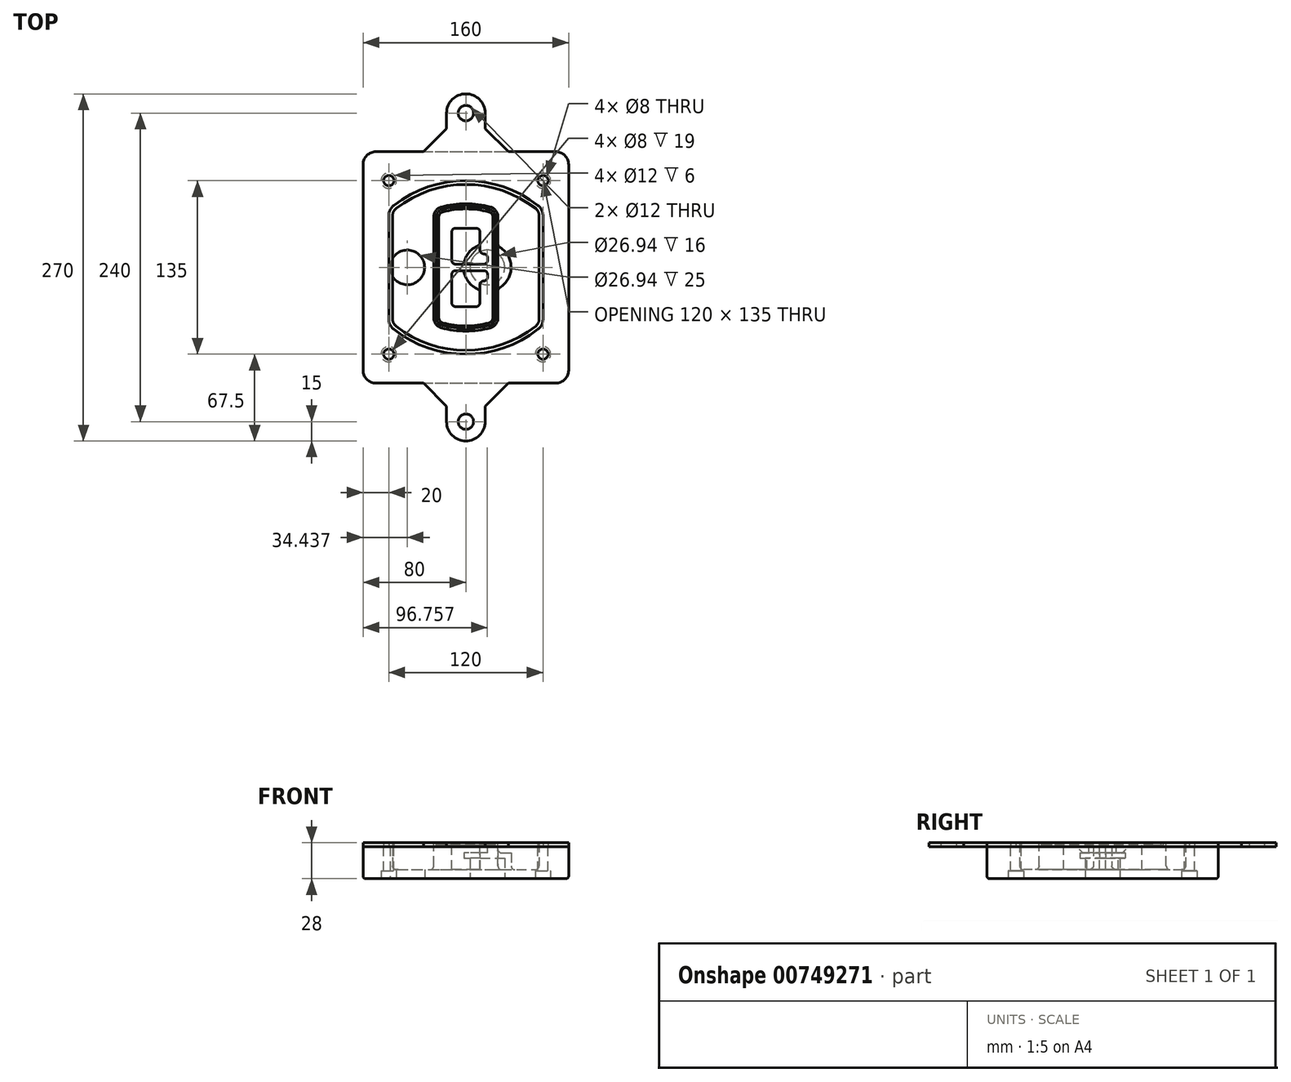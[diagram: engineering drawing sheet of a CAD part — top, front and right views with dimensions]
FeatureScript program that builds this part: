
annotation { "Feature Type Name" : "Feature", "Feature Type Description" : "" }
export const myFeature = defineFeature(function(context is Context, id is Id, definition is map)
    precondition{}
    {
        {
            var Q0;
            Q0=qCreatedBy(makeId("Top.planeOp"),FACE);
            var sketch = newSketch(context, id + "F0", { "sketchPlane" : qUnion([Q0])});
            skPoint(sketch, "E0.rect.middle", {"position": v(0, 0) * mm});
            skLineSegment(sketch, "E1.bottom", {"start": v(-70, -90) * mm, "end": v(70, -90) * mm});
            skLineSegment(sketch, "E1.top", {"start": v(-70, 90) * mm, "end": v(70, 90) * mm});
            skLineSegment(sketch, "E1.left", {"start": v(-80, -80) * mm, "end": v(-80, 80) * mm});
            skLineSegment(sketch, "E1.right", {"start": v(80, -80) * mm, "end": v(80, 80) * mm});
            skLineSegment(sketch, "E2", {"start": v(-80, 90) * mm, "end": v(80, -90) * mm, "construction": true});
            skLineSegment(sketch, "E3", {"start": v(80, 90) * mm, "end": v(-80, -90) * mm, "construction": true});
            skCircle(sketch, "E4", {"center": v(-60, 67.5) * mm, "radius": 4 * mm});
            skCircle(sketch, "E5", {"center": v(60, 67.5) * mm, "radius": 4 * mm});
            skCircle(sketch, "E6", {"center": v(60, -67.5) * mm, "radius": 4 * mm});
            skCircle(sketch, "E7", {"center": v(-60, -67.5) * mm, "radius": 4 * mm});
            skLineSegment(sketch, "E8", {"start": v(-60, 67.5) * mm, "end": v(60, 67.5) * mm, "construction": true});
            skLineSegment(sketch, "E9", {"start": v(60, 67.5) * mm, "end": v(60, -67.5) * mm, "construction": true});
            skLineSegment(sketch, "E10", {"start": v(60, -67.5) * mm, "end": v(-60, -67.5) * mm, "construction": true});
            skLineSegment(sketch, "E11", {"start": v(-60, -67.5) * mm, "end": v(-60, 67.5) * mm, "construction": true});
            skLineSegment(sketch, "E12", {"start": v(-60, 40.3) * mm, "end": v(-60, -40.3) * mm});
            skLineSegment(sketch, "E13", {"start": v(60, 40.3) * mm, "end": v(60, -40.3) * mm});
            skArc(sketch, "E14", {"start": v(56.15, 48.18) * mm, "mid": v(0, 67.5) * mm, "end": v(-56.15, 48.18) * mm});
            skArc(sketch, "E15", {"start": v(-56.15, -48.18) * mm, "mid": v(0, -67.5) * mm, "end": v(56.15, -48.18) * mm});
            skLineSegment(sketch, "E16", {"start": v(-60, 0) * mm, "end": v(60, 0) * mm, "construction": true});
            skPoint(sketch, "E17.visualSharp", {"position": v(-60, -45) * mm});
            skArc(sketch, "E17.filletArc", {"start": v(-60, -40.3) * mm, "mid": v(-58.99, -44.68) * mm, "end": v(-56.15, -48.18) * mm});
            skPoint(sketch, "E18.visualSharp", {"position": v(-60, 45) * mm});
            skArc(sketch, "E18.filletArc", {"start": v(-56.15, 48.18) * mm, "mid": v(-58.99, 44.68) * mm, "end": v(-60, 40.3) * mm});
            skPoint(sketch, "E19.visualSharp", {"position": v(60, 45) * mm});
            skArc(sketch, "E19.filletArc", {"start": v(60, 40.3) * mm, "mid": v(58.99, 44.68) * mm, "end": v(56.15, 48.18) * mm});
            skPoint(sketch, "E20.visualSharp", {"position": v(60, -45) * mm});
            skArc(sketch, "E20.filletArc", {"start": v(56.15, -48.18) * mm, "mid": v(58.99, -44.68) * mm, "end": v(60, -40.3) * mm});
            skPoint(sketch, "E21.visualSharp", {"position": v(-80, 90) * mm});
            skArc(sketch, "E21.filletArc", {"start": v(-70, 90) * mm, "mid": v(-77.07, 87.07) * mm, "end": v(-80, 80) * mm});
            skPoint(sketch, "E22.visualSharp", {"position": v(80, 90) * mm});
            skArc(sketch, "E22.filletArc", {"start": v(80, 80) * mm, "mid": v(77.07, 87.07) * mm, "end": v(70, 90) * mm});
            skPoint(sketch, "E23.visualSharp", {"position": v(80, -90) * mm});
            skArc(sketch, "E23.filletArc", {"start": v(70, -90) * mm, "mid": v(77.07, -87.07) * mm, "end": v(80, -80) * mm});
            skPoint(sketch, "E24.visualSharp", {"position": v(-80, -90) * mm});
            skArc(sketch, "E24.filletArc", {"start": v(-80, -80) * mm, "mid": v(-77.07, -87.07) * mm, "end": v(-70, -90) * mm});
            skArc(sketch, "E25.0", {"start": v(57, 40.3) * mm, "mid": v(56.3, 43.36) * mm, "end": v(54.3, 45.81) * mm});
            skLineSegment(sketch, "E25.1", {"start": v(57, 40.3) * mm, "end": v(57, -40.3) * mm});
            skArc(sketch, "E25.2", {"start": v(54.3, -45.81) * mm, "mid": v(56.3, -43.36) * mm, "end": v(57, -40.3) * mm});
            skArc(sketch, "E25.3", {"start": v(-54.3, -45.81) * mm, "mid": v(0, -64.5) * mm, "end": v(54.3, -45.81) * mm});
            skArc(sketch, "E25.4", {"start": v(-57, -40.3) * mm, "mid": v(-56.3, -43.36) * mm, "end": v(-54.3, -45.81) * mm});
            skArc(sketch, "E25.5", {"start": v(54.3, 45.81) * mm, "mid": v(0, 64.5) * mm, "end": v(-54.3, 45.81) * mm});
            skLineSegment(sketch, "E25.6", {"start": v(-57, 40.3) * mm, "end": v(-57, -40.3) * mm});
            skArc(sketch, "E25.7", {"start": v(-54.3, 45.81) * mm, "mid": v(-56.3, 43.36) * mm, "end": v(-57, 40.3) * mm});
            skArc(sketch, "E26.0", {"start": v(-58.62, 51.33) * mm, "mid": v(-62.58, 46.43) * mm, "end": v(-64, 40.3) * mm});
            skArc(sketch, "E26.1", {"start": v(58.62, 51.33) * mm, "mid": v(0, 71.5) * mm, "end": v(-58.62, 51.33) * mm});
            skArc(sketch, "E26.2", {"start": v(64, 40.3) * mm, "mid": v(62.58, 46.43) * mm, "end": v(58.62, 51.33) * mm});
            skLineSegment(sketch, "E26.3", {"start": v(64, 40.3) * mm, "end": v(64, -40.3) * mm});
            skArc(sketch, "E26.4", {"start": v(58.62, -51.33) * mm, "mid": v(62.58, -46.43) * mm, "end": v(64, -40.3) * mm});
            skLineSegment(sketch, "E26.5", {"start": v(-64, 40.3) * mm, "end": v(-64, -40.3) * mm});
            skArc(sketch, "E26.6", {"start": v(-58.62, -51.33) * mm, "mid": v(0, -71.5) * mm, "end": v(58.62, -51.33) * mm});
            skArc(sketch, "E26.7", {"start": v(-64, -40.3) * mm, "mid": v(-62.58, -46.43) * mm, "end": v(-58.62, -51.33) * mm});
            skSolve(sketch);
        }
        {
            var Q0;
            Q0=makeQuery(id+"F0.imprint","IMPRINT",FACE,{"disambiguationData":[TD([[makeQuery(id+"F0.imprint","IMPRINT",EDGE,{"derivedFrom":sQuery(id+"F0.wireOp",EDGE,"E1.bottom")}),1.0]])]});
            var Q1;
            Q1=makeQuery(id+"F0.imprint","IMPRINT",FACE,{"disambiguationData":[TD([[makeQuery(id+"F0.imprint","IMPRINT",EDGE,{"derivedFrom":sQuery(id+"F0.wireOp",EDGE,"E12")}),1.0]])]});
            var Q2;
            Q2=makeQuery(id+"F0.imprint","IMPRINT",FACE,{"disambiguationData":[TD([[makeQuery(id+"F0.imprint","IMPRINT",EDGE,{"derivedFrom":sQuery(id+"F0.wireOp",EDGE,"E25.0")}),1.0]])]});
            var Q3;
            Q3=makeQuery(id+"F0.imprint","IMPRINT",FACE,{"disambiguationData":[TD([[makeQuery(id+"F0.imprint","IMPRINT",EDGE,{"derivedFrom":sQuery(id+"F0.wireOp",EDGE,"E12")}),-1.0]])]});
            extrude(context, id + "F1", {"entities" : qUnion([Q0, Q1, Q2, Q3]), "oppositeDirection" : true, "depth" : 25 * mm});
        }
        {
            var Q0;
            Q0=makeQuery(id+"F0.imprint","IMPRINT",FACE,{"disambiguationData":[TD([[makeQuery(id+"F0.imprint","IMPRINT",EDGE,{"derivedFrom":sQuery(id+"F0.wireOp",EDGE,"E12")}),1.0]])]});
            extrude(context, id + "F2", {"entities" : qUnion([Q0]), "operationType" : NewBodyOperationType.ADD, "depth" : 3 * mm});
        }
        {
            var Q0;
            Q0=makeQuery(id+"F0.imprint","IMPRINT",FACE,{"disambiguationData":[TD([[makeQuery(id+"F0.imprint","IMPRINT",EDGE,{"derivedFrom":sQuery(id+"F0.wireOp",EDGE,"E25.0")}),1.0]])]});
            extrude(context, id + "F3", {"entities" : qUnion([Q0]), "operationType" : NewBodyOperationType.REMOVE, "oppositeDirection" : true, "depth" : 18 * mm});
        }
        {
            var Q0;
            Q0=makeQuery(id+"F2.opExtrude","CAP_FACE",FACE,{"disambiguationData":[OSD([sQuery(id+"F0.wireOp",EDGE,"E12"),sQuery(id+"F0.wireOp",EDGE,"E13"),sQuery(id+"F0.wireOp",EDGE,"E14"),sQuery(id+"F0.wireOp",EDGE,"E15"),sQuery(id+"F0.wireOp",EDGE,"E17.filletArc"),sQuery(id+"F0.wireOp",EDGE,"E18.filletArc"),sQuery(id+"F0.wireOp",EDGE,"E19.filletArc"),sQuery(id+"F0.wireOp",EDGE,"E20.filletArc"),sQuery(id+"F0.wireOp",EDGE,"E25.0"),sQuery(id+"F0.wireOp",EDGE,"E25.1"),sQuery(id+"F0.wireOp",EDGE,"E25.2"),sQuery(id+"F0.wireOp",EDGE,"E25.3"),sQuery(id+"F0.wireOp",EDGE,"E25.4"),sQuery(id+"F0.wireOp",EDGE,"E25.5"),sQuery(id+"F0.wireOp",EDGE,"E25.6"),sQuery(id+"F0.wireOp",EDGE,"E25.7")])],"isStart":false});
            var sketch = newSketch(context, id + "F4", { "sketchPlane" : qUnion([Q0])});
            skArc(sketch, "E27.0", {"start": v(-19.08, -46.97) * mm, "mid": v(0, -49.5) * mm, "end": v(19.08, -46.97) * mm});
            skArc(sketch, "E28.0", {"start": v(19.08, 46.97) * mm, "mid": v(0, 49.5) * mm, "end": v(-19.08, 46.97) * mm});
            skLineSegment(sketch, "E29", {"start": v(-25, 39.25) * mm, "end": v(-25, -39.25) * mm});
            skLineSegment(sketch, "E30", {"start": v(25, 39.25) * mm, "end": v(25, -39.25) * mm});
            skLineSegment(sketch, "E31", {"start": v(-25, 45.1) * mm, "end": v(25, 45.1) * mm, "construction": true});
            skLineSegment(sketch, "E32", {"start": v(-25, -45.1) * mm, "end": v(25, -45.1) * mm, "construction": true});
            skPoint(sketch, "E33.visualSharp", {"position": v(-25, 45.1) * mm});
            skArc(sketch, "E33.filletArc", {"start": v(-19.08, 46.97) * mm, "mid": v(-23.35, 44.11) * mm, "end": v(-25, 39.25) * mm});
            skPoint(sketch, "E34.visualSharp", {"position": v(25, 45.1) * mm});
            skArc(sketch, "E34.filletArc", {"start": v(25, 39.25) * mm, "mid": v(23.35, 44.11) * mm, "end": v(19.08, 46.97) * mm});
            skPoint(sketch, "E35.visualSharp", {"position": v(25, -45.1) * mm});
            skArc(sketch, "E35.filletArc", {"start": v(19.08, -46.97) * mm, "mid": v(23.35, -44.11) * mm, "end": v(25, -39.25) * mm});
            skPoint(sketch, "E36.visualSharp", {"position": v(-25, -45.1) * mm});
            skArc(sketch, "E36.filletArc", {"start": v(-25, -39.25) * mm, "mid": v(-23.35, -44.11) * mm, "end": v(-19.08, -46.97) * mm});
            skArc(sketch, "E37.0", {"start": v(54.3, 45.81) * mm, "mid": v(0, 64.5) * mm, "end": v(-54.3, 45.81) * mm});
            skArc(sketch, "E37.1", {"start": v(-54.3, 45.81) * mm, "mid": v(-56.3, 43.36) * mm, "end": v(-57, 40.3) * mm});
            skLineSegment(sketch, "E37.2", {"start": v(-57, 40.3) * mm, "end": v(-57, -40.3) * mm});
            skArc(sketch, "E37.3", {"start": v(-57, -40.3) * mm, "mid": v(-56.3, -43.36) * mm, "end": v(-54.3, -45.81) * mm});
            skArc(sketch, "E37.4", {"start": v(-54.3, -45.81) * mm, "mid": v(0, -64.5) * mm, "end": v(54.3, -45.81) * mm});
            skArc(sketch, "E37.5", {"start": v(54.3, -45.81) * mm, "mid": v(56.3, -43.36) * mm, "end": v(57, -40.3) * mm});
            skLineSegment(sketch, "E37.6", {"start": v(57, 40.3) * mm, "end": v(57, -40.3) * mm});
            skArc(sketch, "E37.7", {"start": v(57, 40.3) * mm, "mid": v(56.3, 43.36) * mm, "end": v(54.3, 45.81) * mm});
            skLineSegment(sketch, "E38.0", {"start": v(23, 39.25) * mm, "end": v(23, -39.25) * mm});
            skArc(sketch, "E38.1", {"start": v(18.56, -45.04) * mm, "mid": v(21.76, -42.9) * mm, "end": v(23, -39.25) * mm});
            skArc(sketch, "E38.2", {"start": v(-18.56, -45.04) * mm, "mid": v(0, -47.5) * mm, "end": v(18.56, -45.04) * mm});
            skArc(sketch, "E38.3", {"start": v(-23, -39.25) * mm, "mid": v(-21.76, -42.9) * mm, "end": v(-18.56, -45.04) * mm});
            skLineSegment(sketch, "E38.4", {"start": v(-23, 39.25) * mm, "end": v(-23, -39.25) * mm});
            skArc(sketch, "E38.5", {"start": v(23, 39.25) * mm, "mid": v(21.76, 42.9) * mm, "end": v(18.56, 45.04) * mm});
            skArc(sketch, "E38.6", {"start": v(-18.56, 45.04) * mm, "mid": v(-21.76, 42.9) * mm, "end": v(-23, 39.25) * mm});
            skArc(sketch, "E38.7", {"start": v(18.56, 45.04) * mm, "mid": v(0, 47.5) * mm, "end": v(-18.56, 45.04) * mm});
            skArc(sketch, "E39.0", {"start": v(21, 39.25) * mm, "mid": v(20.18, 41.68) * mm, "end": v(18.04, 43.1) * mm});
            skLineSegment(sketch, "E39.1", {"start": v(21, 39.25) * mm, "end": v(21, -39.25) * mm});
            skArc(sketch, "E39.2", {"start": v(18.04, -43.1) * mm, "mid": v(20.18, -41.68) * mm, "end": v(21, -39.25) * mm});
            skArc(sketch, "E39.3", {"start": v(-18.04, -43.1) * mm, "mid": v(0, -45.5) * mm, "end": v(18.04, -43.1) * mm});
            skArc(sketch, "E39.4", {"start": v(-21, -39.25) * mm, "mid": v(-20.18, -41.68) * mm, "end": v(-18.04, -43.1) * mm});
            skArc(sketch, "E39.5", {"start": v(18.04, 43.1) * mm, "mid": v(0, 45.5) * mm, "end": v(-18.04, 43.1) * mm});
            skLineSegment(sketch, "E39.6", {"start": v(-21, 39.25) * mm, "end": v(-21, -39.25) * mm});
            skArc(sketch, "E39.7", {"start": v(-18.04, 43.1) * mm, "mid": v(-20.18, 41.68) * mm, "end": v(-21, 39.25) * mm});
            skLineSegment(sketch, "E40", {"start": v(-25, 0) * mm, "end": v(25, 0) * mm, "construction": true});
            skLineSegment(sketch, "E41", {"start": v(-11, 5.5) * mm, "end": v(-11, 27.5) * mm});
            skLineSegment(sketch, "E42", {"start": v(-8, 30.5) * mm, "end": v(8, 30.5) * mm});
            skLineSegment(sketch, "E43", {"start": v(11, 27.5) * mm, "end": v(11, 13.5) * mm});
            skLineSegment(sketch, "E44", {"start": v(14, 10.5) * mm, "end": v(14, 10.5) * mm});
            skLineSegment(sketch, "E45", {"start": v(17, 7.5) * mm, "end": v(17, 5.5) * mm});
            skLineSegment(sketch, "E46", {"start": v(14, 2.5) * mm, "end": v(-8, 2.5) * mm});
            skPoint(sketch, "E47.visualSharp", {"position": v(-11, 30.5) * mm});
            skArc(sketch, "E47.filletArc", {"start": v(-8, 30.5) * mm, "mid": v(-10.12, 29.62) * mm, "end": v(-11, 27.5) * mm});
            skPoint(sketch, "E48.visualSharp", {"position": v(11, 30.5) * mm});
            skArc(sketch, "E48.filletArc", {"start": v(11, 27.5) * mm, "mid": v(10.12, 29.62) * mm, "end": v(8, 30.5) * mm});
            skPoint(sketch, "E49.visualSharp", {"position": v(11, 10.5) * mm});
            skArc(sketch, "E49.filletArc", {"start": v(11, 13.5) * mm, "mid": v(11.88, 11.38) * mm, "end": v(14, 10.5) * mm});
            skPoint(sketch, "E50.visualSharp", {"position": v(17, 10.5) * mm});
            skArc(sketch, "E50.filletArc", {"start": v(17, 7.5) * mm, "mid": v(16.12, 9.62) * mm, "end": v(14, 10.5) * mm});
            skPoint(sketch, "E51.visualSharp", {"position": v(17, 2.5) * mm});
            skArc(sketch, "E51.filletArc", {"start": v(14, 2.5) * mm, "mid": v(16.12, 3.38) * mm, "end": v(17, 5.5) * mm});
            skPoint(sketch, "E52.visualSharp", {"position": v(-11, 2.5) * mm});
            skArc(sketch, "E52.filletArc", {"start": v(-11, 5.5) * mm, "mid": v(-10.12, 3.38) * mm, "end": v(-8, 2.5) * mm});
            skLineSegment(sketch, "E53.0.MirrorCS", {"start": v(14, -2.5) * mm, "end": v(-8, -2.5) * mm});
            skArc(sketch, "E54.0.MirrorCS", {"start": v(-11, -5.5) * mm, "mid": v(-10.12, -3.38) * mm, "end": v(-8, -2.5) * mm});
            skLineSegment(sketch, "E55.0.MirrorCS", {"start": v(-11, -5.5) * mm, "end": v(-11, -27.5) * mm});
            skArc(sketch, "E56.0.MirrorCS", {"start": v(-8, -30.5) * mm, "mid": v(-10.12, -29.62) * mm, "end": v(-11, -27.5) * mm});
            skLineSegment(sketch, "E57.0.MirrorCS", {"start": v(-8, -30.5) * mm, "end": v(8, -30.5) * mm});
            skArc(sketch, "E58.0.MirrorCS", {"start": v(11, -27.5) * mm, "mid": v(10.12, -29.62) * mm, "end": v(8, -30.5) * mm});
            skLineSegment(sketch, "E59.0.MirrorCS", {"start": v(11, -27.5) * mm, "end": v(11, -13.5) * mm});
            skArc(sketch, "E60.0.MirrorCS", {"start": v(11, -13.5) * mm, "mid": v(11.88, -11.38) * mm, "end": v(14, -10.5) * mm});
            skArc(sketch, "E61.0.MirrorCS", {"start": v(17, -7.5) * mm, "mid": v(16.12, -9.62) * mm, "end": v(14, -10.5) * mm});
            skLineSegment(sketch, "E62.0.MirrorCS", {"start": v(17, -7.5) * mm, "end": v(17, -5.5) * mm});
            skArc(sketch, "E63.0.MirrorCS", {"start": v(14, -2.5) * mm, "mid": v(16.12, -3.38) * mm, "end": v(17, -5.5) * mm});
            skSolve(sketch);
        }
        {
            var Q0;
            Q0=makeQuery(id+"F4.imprint","IMPRINT",FACE,{"disambiguationData":[TD([[makeQuery(id+"F4.imprint","IMPRINT",EDGE,{"derivedFrom":sQuery(id+"F4.wireOp",EDGE,"E27.0")}),1.0]])]});
            var Q1;
            Q1=makeQuery(id+"F4.imprint","IMPRINT",FACE,{"disambiguationData":[TD([[makeQuery(id+"F4.imprint","IMPRINT",EDGE,{"derivedFrom":sQuery(id+"F4.wireOp",EDGE,"E38.0")}),-1.0]])]});
            var Q2;
            Q2=makeQuery(id+"F4.imprint","IMPRINT",FACE,{"disambiguationData":[TD([[makeQuery(id+"F4.imprint","IMPRINT",EDGE,{"derivedFrom":sQuery(id+"F4.wireOp",EDGE,"E39.0")}),1.0]])]});
            extrude(context, id + "F5", {"entities" : qUnion([Q0, Q1, Q2]), "operationType" : NewBodyOperationType.ADD, "endBound" : BoundingType.UP_TO_NEXT, "oppositeDirection" : true, "depth" : 25 * mm});
        }
        {
            var Q0;
            Q0=makeQuery(id+"F4.imprint","IMPRINT",FACE,{"disambiguationData":[TD([[makeQuery(id+"F4.imprint","IMPRINT",EDGE,{"derivedFrom":sQuery(id+"F4.wireOp",EDGE,"E38.0")}),-1.0]])]});
            extrude(context, id + "F6", {"entities" : qUnion([Q0]), "operationType" : NewBodyOperationType.REMOVE, "oppositeDirection" : true, "depth" : 2 * mm});
        }
        {
            var Q0;
            Q0=makeQuery(id+"F1.opExtrude","CAP_FACE",FACE,{"disambiguationData":[OSD([sQuery(id+"F0.wireOp",EDGE,"E1.bottom"),sQuery(id+"F0.wireOp",EDGE,"E1.top"),sQuery(id+"F0.wireOp",EDGE,"E1.left"),sQuery(id+"F0.wireOp",EDGE,"E1.right"),sQuery(id+"F0.wireOp",EDGE,"E4"),sQuery(id+"F0.wireOp",EDGE,"E5"),sQuery(id+"F0.wireOp",EDGE,"E6"),sQuery(id+"F0.wireOp",EDGE,"E7"),sQuery(id+"F0.wireOp",EDGE,"E21.filletArc"),sQuery(id+"F0.wireOp",EDGE,"E22.filletArc"),sQuery(id+"F0.wireOp",EDGE,"E23.filletArc"),sQuery(id+"F0.wireOp",EDGE,"E24.filletArc")])],"isStart":false});
            var sketch = newSketch(context, id + "F7", { "sketchPlane" : qUnion([Q0])});
            skCircle(sketch, "E64", {"center": v(16.76, 0) * mm, "radius": 13.47 * mm});
            skCircle(sketch, "E65", {"center": v(-45.56, 0) * mm, "radius": 13.47 * mm});
            skLineSegment(sketch, "E66", {"start": v(80, 0) * mm, "end": v(-80, 0) * mm});
            skCircle(sketch, "E67", {"center": v(16.76, 0) * mm, "radius": 18.47 * mm});
            skCircle(sketch, "E68", {"center": v(60, -67.5) * mm, "radius": 6 * mm});
            skCircle(sketch, "E69", {"center": v(-60, -67.5) * mm, "radius": 6 * mm});
            skCircle(sketch, "E70", {"center": v(-60, 67.5) * mm, "radius": 6 * mm});
            skCircle(sketch, "E71", {"center": v(60, 67.5) * mm, "radius": 6 * mm});
            skSolve(sketch);
        }
        {
            var Q0;
            {var subQ1=sQuery(id+"F7.wireOp",EDGE,"E66");var subQ4=sQuery(id+"F7.wireOp",EDGE,"E64");var subQ6=makeQuery(id+"F7.imprint","INTERSECT",VERTEX,{"disambiguationData":[OD(0.0)],"derivedFrom":[subQ4,subQ1]});Q0=makeQuery(id+"F7.imprint","IMPRINT",FACE,{"disambiguationData":[TD([[makeQuery(id+"F7.imprint","IMPRINT",EDGE,{"disambiguationData":[TD([[subQ6,-1.0]])],"derivedFrom":subQ4}),-1.0]])]});}
            var Q1;
            {var subQ0=sQuery(id+"F7.wireOp",EDGE,"E66");var subQ1=sQuery(id+"F7.wireOp",EDGE,"E64");var subQ3=makeQuery(id+"F7.imprint","INTERSECT",VERTEX,{"disambiguationData":[OD(0.0)],"derivedFrom":[subQ1,subQ0]});Q1=makeQuery(id+"F7.imprint","IMPRINT",FACE,{"disambiguationData":[TD([[makeQuery(id+"F7.imprint","IMPRINT",EDGE,{"disambiguationData":[TD([[subQ3,-1.0]])],"derivedFrom":subQ1}),1.0]])]});}
            var Q2;
            {var subQ0=sQuery(id+"F7.wireOp",EDGE,"E66");var subQ1=sQuery(id+"F7.wireOp",EDGE,"E64");var subQ3=makeQuery(id+"F7.imprint","INTERSECT",VERTEX,{"disambiguationData":[OD(0.0)],"derivedFrom":[subQ1,subQ0]});Q2=makeQuery(id+"F7.imprint","IMPRINT",FACE,{"disambiguationData":[TD([[makeQuery(id+"F7.imprint","IMPRINT",EDGE,{"disambiguationData":[TD([[subQ3,1.0]])],"derivedFrom":subQ1}),1.0]])]});}
            var Q3;
            {var subQ1=sQuery(id+"F7.wireOp",EDGE,"E66");var subQ4=sQuery(id+"F7.wireOp",EDGE,"E64");var subQ6=makeQuery(id+"F7.imprint","INTERSECT",VERTEX,{"disambiguationData":[OD(0.0)],"derivedFrom":[subQ4,subQ1]});Q3=makeQuery(id+"F7.imprint","IMPRINT",FACE,{"disambiguationData":[TD([[makeQuery(id+"F7.imprint","IMPRINT",EDGE,{"disambiguationData":[TD([[subQ6,1.0]])],"derivedFrom":subQ4}),-1.0]])]});}
            extrude(context, id + "F8", {"entities" : qUnion([Q0, Q1, Q2, Q3]), "operationType" : NewBodyOperationType.ADD, "oppositeDirection" : true, "depth" : 20 * mm});
        }
        {
            var Q0;
            {var subQ0=sQuery(id+"F7.wireOp",EDGE,"E66");var subQ1=sQuery(id+"F7.wireOp",EDGE,"E64");var subQ3=makeQuery(id+"F7.imprint","INTERSECT",VERTEX,{"disambiguationData":[OD(0.0)],"derivedFrom":[subQ1,subQ0]});Q0=makeQuery(id+"F7.imprint","IMPRINT",FACE,{"disambiguationData":[TD([[makeQuery(id+"F7.imprint","IMPRINT",EDGE,{"disambiguationData":[TD([[subQ3,-1.0]])],"derivedFrom":subQ1}),1.0]])]});}
            var Q1;
            {var subQ0=sQuery(id+"F7.wireOp",EDGE,"E66");var subQ1=sQuery(id+"F7.wireOp",EDGE,"E64");var subQ3=makeQuery(id+"F7.imprint","INTERSECT",VERTEX,{"disambiguationData":[OD(0.0)],"derivedFrom":[subQ1,subQ0]});Q1=makeQuery(id+"F7.imprint","IMPRINT",FACE,{"disambiguationData":[TD([[makeQuery(id+"F7.imprint","IMPRINT",EDGE,{"disambiguationData":[TD([[subQ3,1.0]])],"derivedFrom":subQ1}),1.0]])]});}
            extrude(context, id + "F9", {"entities" : qUnion([Q0, Q1]), "operationType" : NewBodyOperationType.REMOVE, "oppositeDirection" : true, "depth" : 16 * mm});
        }
        {
            var Q0;
            {var subQ0=sQuery(id+"F7.wireOp",EDGE,"E66");var subQ1=sQuery(id+"F7.wireOp",EDGE,"E65");var subQ3=makeQuery(id+"F7.imprint","INTERSECT",VERTEX,{"disambiguationData":[OD(0.0)],"derivedFrom":[subQ1,subQ0]});Q0=makeQuery(id+"F7.imprint","IMPRINT",FACE,{"disambiguationData":[TD([[makeQuery(id+"F7.imprint","IMPRINT",EDGE,{"disambiguationData":[TD([[subQ3,-1.0]])],"derivedFrom":subQ1}),1.0]])]});}
            var Q1;
            {var subQ0=sQuery(id+"F7.wireOp",EDGE,"E66");var subQ1=sQuery(id+"F7.wireOp",EDGE,"E65");var subQ3=makeQuery(id+"F7.imprint","INTERSECT",VERTEX,{"disambiguationData":[OD(0.0)],"derivedFrom":[subQ1,subQ0]});Q1=makeQuery(id+"F7.imprint","IMPRINT",FACE,{"disambiguationData":[TD([[makeQuery(id+"F7.imprint","IMPRINT",EDGE,{"disambiguationData":[TD([[subQ3,1.0]])],"derivedFrom":subQ1}),1.0]])]});}
            extrude(context, id + "F10", {"entities" : qUnion([Q0, Q1]), "operationType" : NewBodyOperationType.REMOVE, "oppositeDirection" : true, "depth" : 25 * mm});
        }
        {
            var Q0;
            Q0=makeQuery(id+"F7.imprint","IMPRINT",FACE,{"disambiguationData":[TD([[makeQuery(id+"F7.imprint","IMPRINT",EDGE,{"derivedFrom":sQuery(id+"F7.wireOp",EDGE,"E68")}),1.0]])]});
            var Q1;
            Q1=makeQuery(id+"F7.imprint","IMPRINT",FACE,{"disambiguationData":[TD([[makeQuery(id+"F7.imprint","IMPRINT",EDGE,{"derivedFrom":makeQuery(id+"F1.opExtrude","CAP_EDGE",EDGE,{"disambiguationData":[OSD([sQuery(id+"F0.wireOp",EDGE,"E5")])],"isStart":false})}),-1.0]])]});
            var Q2;
            Q2=makeQuery(id+"F7.imprint","IMPRINT",FACE,{"disambiguationData":[TD([[makeQuery(id+"F7.imprint","IMPRINT",EDGE,{"derivedFrom":sQuery(id+"F7.wireOp",EDGE,"E69")}),1.0]])]});
            var Q3;
            Q3=makeQuery(id+"F7.imprint","IMPRINT",FACE,{"disambiguationData":[TD([[makeQuery(id+"F7.imprint","IMPRINT",EDGE,{"derivedFrom":makeQuery(id+"F1.opExtrude","CAP_EDGE",EDGE,{"disambiguationData":[OSD([sQuery(id+"F0.wireOp",EDGE,"E4")])],"isStart":false})}),-1.0]])]});
            var Q4;
            Q4=makeQuery(id+"F7.imprint","IMPRINT",FACE,{"disambiguationData":[TD([[makeQuery(id+"F7.imprint","IMPRINT",EDGE,{"derivedFrom":sQuery(id+"F7.wireOp",EDGE,"E70")}),1.0]])]});
            var Q5;
            Q5=makeQuery(id+"F7.imprint","IMPRINT",FACE,{"disambiguationData":[TD([[makeQuery(id+"F7.imprint","IMPRINT",EDGE,{"derivedFrom":makeQuery(id+"F1.opExtrude","CAP_EDGE",EDGE,{"disambiguationData":[OSD([sQuery(id+"F0.wireOp",EDGE,"E7")])],"isStart":false})}),-1.0]])]});
            var Q6;
            Q6=makeQuery(id+"F7.imprint","IMPRINT",FACE,{"disambiguationData":[TD([[makeQuery(id+"F7.imprint","IMPRINT",EDGE,{"derivedFrom":sQuery(id+"F7.wireOp",EDGE,"E71")}),1.0]])]});
            var Q7;
            Q7=makeQuery(id+"F7.imprint","IMPRINT",FACE,{"disambiguationData":[TD([[makeQuery(id+"F7.imprint","IMPRINT",EDGE,{"derivedFrom":makeQuery(id+"F1.opExtrude","CAP_EDGE",EDGE,{"disambiguationData":[OSD([sQuery(id+"F0.wireOp",EDGE,"E6")])],"isStart":false})}),-1.0]])]});
            extrude(context, id + "F11", {"entities" : qUnion([Q0, Q1, Q2, Q3, Q4, Q5, Q6, Q7]), "operationType" : NewBodyOperationType.REMOVE, "oppositeDirection" : true, "depth" : 6 * mm});
        }
        {
            var Q0;
            Q0=makeQuery(id+"F9.boolean.opBoolean","COPY",FACE,{"derivedFrom":makeQuery(id+"F9.opExtrude","CAP_FACE",FACE,{"disambiguationData":[OSD([sQuery(id+"F7.wireOp",EDGE,"E64")])],"isStart":false})});
            var sketch = newSketch(context, id + "F12", { "sketchPlane" : qUnion([Q0])});
            skArc(sketch, "E72.0", {"start": v(11, 17.55) * mm, "mid": v(2.57, 11.82) * mm, "end": v(-1.54, 2.5) * mm});
            skArc(sketch, "E72.1", {"start": v(-1.54, -2.5) * mm, "mid": v(2.57, -11.82) * mm, "end": v(11, -17.55) * mm});
            skLineSegment(sketch, "E73", {"start": v(-1.54, -2.5) * mm, "end": v(14, -2.5) * mm});
            skLineSegment(sketch, "E74.0", {"start": v(14, 2.5) * mm, "end": v(-1.54, 2.5) * mm});
            skArc(sketch, "E74.1", {"start": v(14, 2.5) * mm, "mid": v(16.12, 3.38) * mm, "end": v(17, 5.5) * mm});
            skLineSegment(sketch, "E74.2", {"start": v(17, 7.5) * mm, "end": v(17, 5.5) * mm});
            skArc(sketch, "E74.3", {"start": v(17, 7.5) * mm, "mid": v(16.12, 9.62) * mm, "end": v(14, 10.5) * mm});
            skArc(sketch, "E74.4", {"start": v(11, 13.5) * mm, "mid": v(11.88, 11.38) * mm, "end": v(14, 10.5) * mm});
            skLineSegment(sketch, "E74.5", {"start": v(11, 17.55) * mm, "end": v(11, 13.5) * mm});
            skLineSegment(sketch, "E74.7", {"start": v(14, -2.5) * mm, "end": v(-1.54, -2.5) * mm});
            skArc(sketch, "E74.8", {"start": v(14, -2.5) * mm, "mid": v(16.12, -3.38) * mm, "end": v(17, -5.5) * mm});
            skLineSegment(sketch, "E74.9", {"start": v(17, -7.5) * mm, "end": v(17, -5.5) * mm});
            skArc(sketch, "E74.10", {"start": v(17, -7.5) * mm, "mid": v(16.12, -9.62) * mm, "end": v(14, -10.5) * mm});
            skArc(sketch, "E74.11", {"start": v(11, -13.5) * mm, "mid": v(11.88, -11.38) * mm, "end": v(14, -10.5) * mm});
            skLineSegment(sketch, "E74.12", {"start": v(11, -17.55) * mm, "end": v(11, -13.5) * mm});
            skPoint(sketch, "E75.orphan", {"position": v(11, -27.5) * mm});
            skPoint(sketch, "E76.orphan", {"position": v(-8, -2.5) * mm});
            skPoint(sketch, "E77.orphan", {"position": v(-8, 2.5) * mm});
            skPoint(sketch, "E78.orphan", {"position": v(11, 27.5) * mm});
            skSolve(sketch);
        }
        {
            var Q0;
            {var subQ7=sQuery(id+"F12.wireOp",EDGE,"E72.0");var subQ14=sQuery(id+"F12.wireOp",EDGE,"E72.1");var subQ16=sQuery(id+"F12.wireOp",EDGE,"E74.1");var subQ18=sQuery(id+"F12.wireOp",EDGE,"E74.8");Q0=qUnion([makeQuery(id+"F12.imprint","IMPRINT",FACE,{"disambiguationData":[TD([[makeQuery(id+"F12.imprint","IMPRINT",EDGE,{"derivedFrom":subQ7}),1.0]])]}),makeQuery(id+"F12.imprint","IMPRINT",FACE,{"disambiguationData":[TD([[makeQuery(id+"F12.imprint","IMPRINT",EDGE,{"derivedFrom":subQ14}),1.0]])]}),makeQuery(id+"F12.imprint","IMPRINT",FACE,{"disambiguationData":[TD([[makeQuery(id+"F12.imprint","IMPRINT",EDGE,{"derivedFrom":subQ16}),1.0]])]}),makeQuery(id+"F12.imprint","IMPRINT",FACE,{"disambiguationData":[TD([[makeQuery(id+"F12.imprint","IMPRINT",EDGE,{"derivedFrom":subQ18}),-1.0]])]})]);}
            var Q1;
            Q1=makeQuery(id+"F5.boolean.opBoolean","SPLIT",FACE,{"disambiguationData":[TD([makeQuery(id+"F5.opExtrude","SWEPT_FACE",FACE,{"disambiguationData":[OSD([sQuery(id+"F4.wireOp",EDGE,"E41")])]})])],"derivedFrom":makeQuery(id+"F3.boolean.opBoolean","COPY",FACE,{"derivedFrom":makeQuery(id+"F3.opExtrude","CAP_FACE",FACE,{"disambiguationData":[OSD([sQuery(id+"F0.wireOp",EDGE,"E25.0"),sQuery(id+"F0.wireOp",EDGE,"E25.1"),sQuery(id+"F0.wireOp",EDGE,"E25.2"),sQuery(id+"F0.wireOp",EDGE,"E25.3"),sQuery(id+"F0.wireOp",EDGE,"E25.4"),sQuery(id+"F0.wireOp",EDGE,"E25.5"),sQuery(id+"F0.wireOp",EDGE,"E25.6"),sQuery(id+"F0.wireOp",EDGE,"E25.7")])],"isStart":false})})});
            extrude(context, id + "F13", {"entities" : qUnion([Q0]), "operationType" : NewBodyOperationType.REMOVE, "endBound" : BoundingType.UP_TO_SURFACE, "endBoundEntityFace" : qUnion([Q1]), "depth" : 25 * mm});
        }
        {
            var Q0;
            Q0=makeQuery(id+"F3.boolean.opBoolean","COPY",EDGE,{"derivedFrom":makeQuery(id+"F3.opExtrude","CAP_EDGE",EDGE,{"disambiguationData":[OSD([sQuery(id+"F0.wireOp",EDGE,"E25.6")])],"isStart":false})});
            var Q1;
            Q1=makeQuery(id+"F8.boolean.opBoolean","INTERSECT",EDGE,{"derivedFrom":[makeQuery(id+"F5.opExtrude","SWEPT_FACE",FACE,{"disambiguationData":[OSD([sQuery(id+"F4.wireOp",EDGE,"E30")])]}),makeQuery(id+"F8.opExtrude","CAP_FACE",FACE,{"disambiguationData":[OSD([sQuery(id+"F7.wireOp",EDGE,"E67")])],"isStart":false})]});
            var Q2;
            Q2=makeQuery(id+"F8.boolean.opBoolean","INTERSECT",EDGE,{"disambiguationData":[OD(1.0)],"derivedFrom":[makeQuery(id+"F5.opExtrude","SWEPT_FACE",FACE,{"disambiguationData":[OSD([sQuery(id+"F4.wireOp",EDGE,"E30")])]}),makeQuery(id+"F8.opExtrude","SWEPT_FACE",FACE,{"disambiguationData":[OSD([sQuery(id+"F7.wireOp",EDGE,"E67")])]})]});
            var Q3;
            {var subQ0=sQuery(id+"F4.wireOp",EDGE,"E30");Q3=makeQuery(id+"F8.boolean.opBoolean","SPLIT",EDGE,{"disambiguationData":[TD([makeQuery(id+"F5.opExtrude","SWEPT_FACE",FACE,{"disambiguationData":[OSD([sQuery(id+"F4.wireOp",EDGE,"E35.filletArc")])]})])],"derivedFrom":makeQuery(id+"F5.opExtrude","CAP_EDGE",EDGE,{"disambiguationData":[OSD([subQ0])],"isStart":false})});}
            var Q4;
            {var subQ0=sQuery(id+"F0.wireOp",EDGE,"E25.7");var subQ1=sQuery(id+"F0.wireOp",EDGE,"E25.1");var subQ2=sQuery(id+"F0.wireOp",EDGE,"E25.6");var subQ3=sQuery(id+"F0.wireOp",EDGE,"E25.5");var subQ4=sQuery(id+"F0.wireOp",EDGE,"E25.4");var subQ5=sQuery(id+"F0.wireOp",EDGE,"E25.0");var subQ6=sQuery(id+"F0.wireOp",EDGE,"E25.2");var subQ7=sQuery(id+"F0.wireOp",EDGE,"E25.3");Q4=makeQuery(id+"F8.boolean.opBoolean","INTERSECT",EDGE,{"derivedFrom":[makeQuery(id+"F5.boolean.opBoolean","SPLIT",FACE,{"disambiguationData":[TD([makeQuery(id+"F2.opExtrude","SWEPT_FACE",FACE,{"disambiguationData":[OSD([subQ5])]})])],"derivedFrom":makeQuery(id+"F3.boolean.opBoolean","COPY",FACE,{"derivedFrom":makeQuery(id+"F3.opExtrude","CAP_FACE",FACE,{"disambiguationData":[OSD([subQ5,subQ1,subQ6,subQ7,subQ4,subQ3,subQ2,subQ0])],"isStart":false})})}),makeQuery(id+"F8.opExtrude","SWEPT_FACE",FACE,{"disambiguationData":[OSD([sQuery(id+"F7.wireOp",EDGE,"E67")])]})]});}
            var Q5;
            Q5=makeQuery(id+"F8.boolean.opBoolean","INTERSECT",EDGE,{"disambiguationData":[OD(0.0)],"derivedFrom":[makeQuery(id+"F5.opExtrude","SWEPT_FACE",FACE,{"disambiguationData":[OSD([sQuery(id+"F4.wireOp",EDGE,"E30")])]}),makeQuery(id+"F8.opExtrude","SWEPT_FACE",FACE,{"disambiguationData":[OSD([sQuery(id+"F7.wireOp",EDGE,"E67")])]})]});
            fillet(context, id + "F14", {"entities" : qUnion([Q0, Q1, Q2, Q3, Q4, Q5]), "radius" : 3 * mm, "tangentPropagation" : true, "allowEdgeOverflow" : false});
        }
        {
            var Q0;
            Q0=makeQuery(id+"F1.opExtrude","CAP_EDGE",EDGE,{"disambiguationData":[OSD([sQuery(id+"F0.wireOp",EDGE,"E1.bottom")])],"isStart":false});
            fillet(context, id + "F15", {"entities" : qUnion([Q0]), "radius" : 2 * mm, "tangentPropagation" : true, "allowEdgeOverflow" : false});
        }
        {
            var Q0;
            {var subQ0=sQuery(id+"F0.wireOp",EDGE,"E21.filletArc");var subQ1=sQuery(id+"F0.wireOp",EDGE,"E7");var subQ2=sQuery(id+"F0.wireOp",EDGE,"E6");var subQ3=sQuery(id+"F0.wireOp",EDGE,"E5");var subQ4=sQuery(id+"F0.wireOp",EDGE,"E4");var subQ5=sQuery(id+"F0.wireOp",EDGE,"E22.filletArc");var subQ6=sQuery(id+"F0.wireOp",EDGE,"E1.bottom");var subQ7=sQuery(id+"F0.wireOp",EDGE,"E1.right");var subQ8=sQuery(id+"F0.wireOp",EDGE,"E1.top");var subQ9=sQuery(id+"F0.wireOp",EDGE,"E1.left");var subQ10=sQuery(id+"F0.wireOp",EDGE,"E23.filletArc");var subQ11=sQuery(id+"F0.wireOp",EDGE,"E24.filletArc");Q0=makeQuery(id+"F2.boolean.opBoolean","SPLIT",FACE,{"disambiguationData":[TD([makeQuery(id+"F1.opExtrude","SWEPT_FACE",FACE,{"disambiguationData":[OSD([subQ6])]})])],"derivedFrom":makeQuery(id+"F1.opExtrude","CAP_FACE",FACE,{"disambiguationData":[OSD([subQ6,subQ8,subQ9,subQ7,subQ4,subQ3,subQ2,subQ1,subQ0,subQ5,subQ10,subQ11])],"isStart":true})});}
            var sketch = newSketch(context, id + "F16", { "sketchPlane" : qUnion([Q0])});
            skLineSegment(sketch, "E79", {"start": v(0, 90) * mm, "end": v(0, 120) * mm, "construction": true});
            skCircle(sketch, "E80", {"center": v(0, 120) * mm, "radius": 6 * mm});
            skArc(sketch, "E81", {"start": v(15, 120) * mm, "mid": v(0, 135) * mm, "end": v(-15, 120) * mm});
            skPoint(sketch, "E82.endSnap0", {"position": v(0, 105) * mm});
            skLineSegment(sketch, "E83.0", {"start": v(-70, 90) * mm, "end": v(70, 90) * mm});
            skArc(sketch, "E83.1", {"start": v(-70, 90) * mm, "mid": v(-77.07, 87.07) * mm, "end": v(-80, 80) * mm});
            skLineSegment(sketch, "E83.2", {"start": v(-80, -80) * mm, "end": v(-80, 80) * mm});
            skLineSegment(sketch, "E83.3", {"start": v(-70, -90) * mm, "end": v(70, -90) * mm});
            skLineSegment(sketch, "E83.4", {"start": v(80, -80) * mm, "end": v(80, 80) * mm});
            skArc(sketch, "E83.5", {"start": v(70, -90) * mm, "mid": v(77.07, -87.07) * mm, "end": v(80, -80) * mm});
            skArc(sketch, "E83.6", {"start": v(80, 80) * mm, "mid": v(77.07, 87.07) * mm, "end": v(70, 90) * mm});
            skArc(sketch, "E83.7", {"start": v(-80, -80) * mm, "mid": v(-77.07, -87.07) * mm, "end": v(-70, -90) * mm});
            skArc(sketch, "E83.8", {"start": v(56.15, 48.18) * mm, "mid": v(0, 67.5) * mm, "end": v(-56.15, 48.18) * mm});
            skLineSegment(sketch, "E83.9", {"start": v(-60, 40.3) * mm, "end": v(-60, -40.3) * mm});
            skArc(sketch, "E83.10", {"start": v(-56.15, -48.18) * mm, "mid": v(0, -67.5) * mm, "end": v(56.15, -48.18) * mm});
            skLineSegment(sketch, "E83.11", {"start": v(60, 40.3) * mm, "end": v(60, -40.3) * mm});
            skCircle(sketch, "E83.12", {"center": v(-60, 67.5) * mm, "radius": 4 * mm});
            skCircle(sketch, "E83.13", {"center": v(-60, -67.5) * mm, "radius": 4 * mm});
            skCircle(sketch, "E83.14", {"center": v(60, -67.5) * mm, "radius": 4 * mm});
            skCircle(sketch, "E83.15", {"center": v(60, 67.5) * mm, "radius": 4 * mm});
            skArc(sketch, "E83.16", {"start": v(60, 40.3) * mm, "mid": v(58.99, 44.68) * mm, "end": v(56.15, 48.18) * mm});
            skArc(sketch, "E83.17", {"start": v(-60, -40.3) * mm, "mid": v(-58.99, -44.68) * mm, "end": v(-56.15, -48.18) * mm});
            skArc(sketch, "E83.18", {"start": v(56.15, -48.18) * mm, "mid": v(58.99, -44.68) * mm, "end": v(60, -40.3) * mm});
            skArc(sketch, "E83.19", {"start": v(-56.15, 48.18) * mm, "mid": v(-58.99, 44.68) * mm, "end": v(-60, 40.3) * mm});
            skLineSegment(sketch, "E84", {"start": v(-15, 120) * mm, "end": v(-15, 108) * mm});
            skLineSegment(sketch, "E85", {"start": v(15, 120) * mm, "end": v(15, 108) * mm});
            skLineSegment(sketch, "E86", {"start": v(15, 108) * mm, "end": v(33, 90) * mm});
            skLineSegment(sketch, "E87", {"start": v(-15, 108) * mm, "end": v(-33, 90) * mm});
            skLineSegment(sketch, "E88", {"start": v(-80, 0) * mm, "end": v(80, 0) * mm, "construction": true});
            skLineSegment(sketch, "E89.MirrorCS", {"start": v(15, -108) * mm, "end": v(33, -90) * mm});
            skLineSegment(sketch, "E90.MirrorCS", {"start": v(15, -120) * mm, "end": v(15, -108) * mm});
            skArc(sketch, "E91.MirrorCS", {"start": v(15, -120) * mm, "mid": v(0, -135) * mm, "end": v(-15, -120) * mm});
            skLineSegment(sketch, "E92.MirrorCS", {"start": v(-15, -120) * mm, "end": v(-15, -108) * mm});
            skLineSegment(sketch, "E93.MirrorCS", {"start": v(-15, -108) * mm, "end": v(-33, -90) * mm});
            skCircle(sketch, "E94.MirrorC", {"center": v(0, -120) * mm, "radius": 6 * mm});
            skSolve(sketch);
        }
        {
            var Q0;
            Q0 = qSketchRegion(id + "F16", true);
            var Q1;
            Q1=makeQuery(id+"F2.opExtrude","CAP_FACE",FACE,{"disambiguationData":[OSD([sQuery(id+"F0.wireOp",EDGE,"E12"),sQuery(id+"F0.wireOp",EDGE,"E13"),sQuery(id+"F0.wireOp",EDGE,"E14"),sQuery(id+"F0.wireOp",EDGE,"E15"),sQuery(id+"F0.wireOp",EDGE,"E17.filletArc"),sQuery(id+"F0.wireOp",EDGE,"E18.filletArc"),sQuery(id+"F0.wireOp",EDGE,"E19.filletArc"),sQuery(id+"F0.wireOp",EDGE,"E20.filletArc"),sQuery(id+"F0.wireOp",EDGE,"E25.0"),sQuery(id+"F0.wireOp",EDGE,"E25.1"),sQuery(id+"F0.wireOp",EDGE,"E25.2"),sQuery(id+"F0.wireOp",EDGE,"E25.3"),sQuery(id+"F0.wireOp",EDGE,"E25.4"),sQuery(id+"F0.wireOp",EDGE,"E25.5"),sQuery(id+"F0.wireOp",EDGE,"E25.6"),sQuery(id+"F0.wireOp",EDGE,"E25.7")])],"isStart":false});
            extrude(context, id + "F17", {"entities" : qUnion([Q0]), "endBound" : BoundingType.UP_TO_SURFACE, "depth" : 25 * mm, "endBoundEntityFace" : qUnion([Q1]), "offsetDistance" : 25 * mm});
        }
    });
